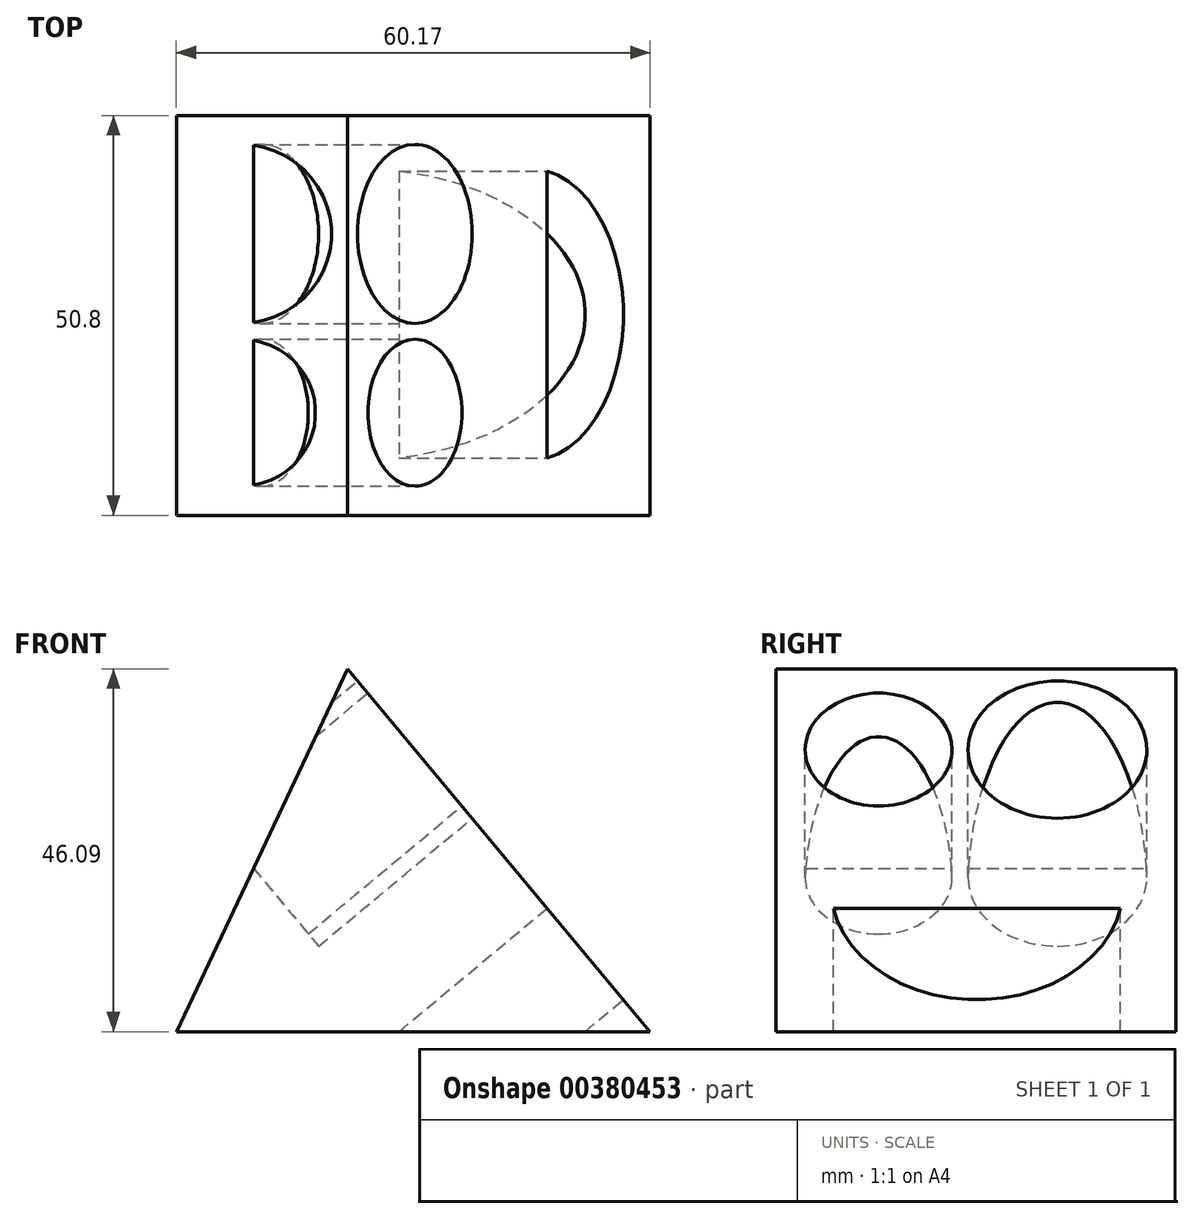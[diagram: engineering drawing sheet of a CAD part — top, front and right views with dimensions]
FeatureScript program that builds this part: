
annotation { "Feature Type Name" : "Feature", "Feature Type Description" : "" }
export const myFeature = defineFeature(function(context is Context, id is Id, definition is map)
    precondition{}
    {
        {
            var Q0;
            Q0=qCreatedBy(makeId("Front.planeOp"),FACE);
            var sketch = newSketch(context, id + "F0", { "sketchPlane" : qUnion([Q0])});
            skLineSegment(sketch, "E0", {"start": v(0, 0) * mm, "end": v(-60.17, 0) * mm});
            skLineSegment(sketch, "E1", {"start": v(-60.17, 0) * mm, "end": v(-38.4, 46.09) * mm});
            skLineSegment(sketch, "E2", {"start": v(-38.4, 46.09) * mm, "end": v(0, 0) * mm});
            skSolve(sketch);
        }
        {
            var Q0;
            Q0 = qSketchRegion(id + "F0", true);
            extrude(context, id + "F1", {"entities" : qUnion([Q0]), "depth" : 50.8 * mm});
        }
        {
            var Q0;
            Q0=makeQuery(id+"F1.opExtrude","SWEPT_FACE",FACE,{"disambiguationData":[OSD([sQuery(id+"F0.wireOp",EDGE,"E2")])]});
            var sketch = newSketch(context, id + "F2", { "sketchPlane" : qUnion([Q0])});
            skCircle(sketch, "E3", {"center": v(-37.76, 46.66) * mm, "radius": 9.33 * mm});
            skCircle(sketch, "E4", {"center": v(-15.04, 46.66) * mm, "radius": 11.37 * mm});
            skLineSegment(sketch, "E5", {"start": v(-43.53, 20.41) * mm, "end": v(-7.04, 20.41) * mm});
            skArc(sketch, "E6", {"start": v(-43.53, 20.41) * mm, "mid": v(-25.28, 5.27) * mm, "end": v(-7.04, 20.41) * mm});
            skSolve(sketch);
        }
        {
            var Q0;
            Q0 = qSketchRegion(id + "F2", true);
            extrude(context, id + "F3", {"entities" : qUnion([Q0]), "operationType" : NewBodyOperationType.REMOVE, "oppositeDirection" : true, "depth" : 25.4 * mm});
        }
    });
